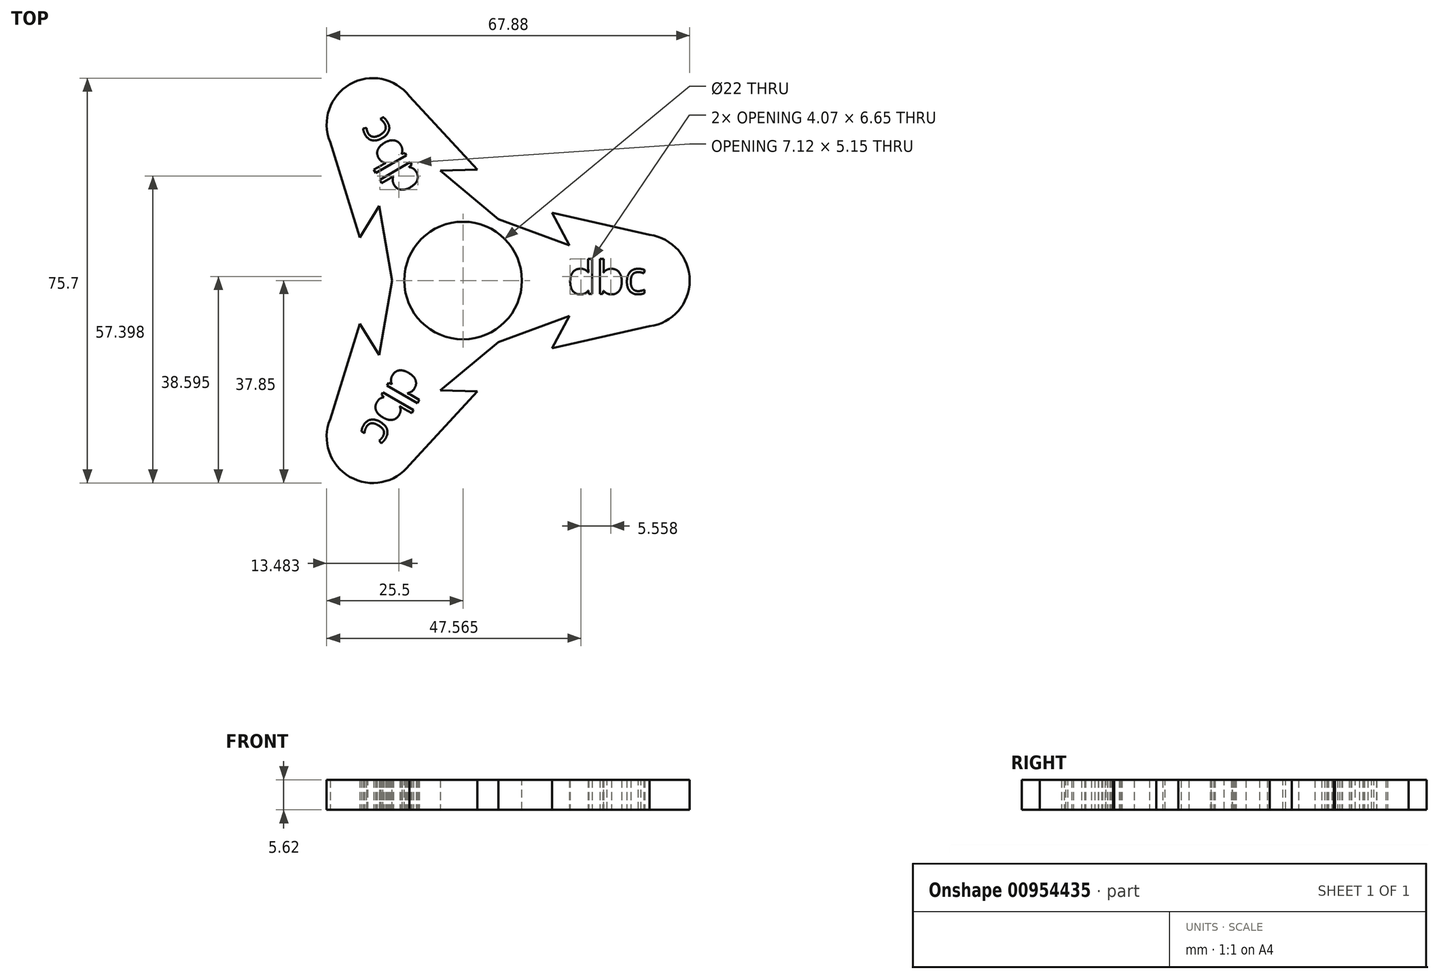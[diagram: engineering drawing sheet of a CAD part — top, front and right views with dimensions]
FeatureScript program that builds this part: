
annotation { "Feature Type Name" : "Feature", "Feature Type Description" : "" }
export const myFeature = defineFeature(function(context is Context, id is Id, definition is map)
    precondition{}
    {
        {
            var Q0;
            Q0=qCreatedBy(makeId("Top.planeOp"),FACE);
            var sketch = newSketch(context, id + "F0", { "sketchPlane" : qUnion([Q0])});
            skCircle(sketch, "E0", {"center": v(0, 0) * mm, "radius": 11 * mm});
            skArc(sketch, "E1", {"start": v(4.51, 16.9) * mm, "mid": v(-17.5, 0) * mm, "end": v(4.51, -16.9) * mm});
            skArc(sketch, "E2", {"start": v(46.5, -11.4) * mm, "mid": v(56.5, 0) * mm, "end": v(46.5, 11.4) * mm});
            skLineSegment(sketch, "E3", {"start": v(0, 17.5) * mm, "end": v(4.51, 16.9) * mm});
            skLineSegment(sketch, "E4", {"start": v(0, -17.5) * mm, "end": v(4.51, -16.9) * mm});
            skLineSegment(sketch, "E5", {"start": v(4.51, -16.9) * mm, "end": v(26.54, -8.8) * mm});
            skLineSegment(sketch, "E6", {"start": v(26.54, -8.8) * mm, "end": v(22.18, -16.9) * mm});
            skLineSegment(sketch, "E7", {"start": v(22.18, -16.9) * mm, "end": v(46.5, -11.4) * mm});
            skLineSegment(sketch, "E8.MirrorCS", {"start": v(4.51, 16.9) * mm, "end": v(26.54, 8.8) * mm});
            skLineSegment(sketch, "E9.MirrorCS", {"start": v(26.54, 8.8) * mm, "end": v(22.18, 16.9) * mm});
            skLineSegment(sketch, "E10.MirrorCS", {"start": v(22.18, 16.9) * mm, "end": v(46.5, 11.4) * mm});
            skText(sketch, "E11", { "text": "dbc\n", "fontName": "OpenSans-Regular.ttf"});
            skLineSegment(sketch, "E12", {"start": v(0, 0) * mm, "end": v(63.02, 0) * mm, "construction": true});
            const initialGuessF0  = {"E11": [0.02606, -0.00333, 1, 0, 0.0083]};
            skSetInitialGuess(sketch, initialGuessF0);
            skSolve(sketch);
        }
        {
            var Q0;
            Q0 = qSketchRegion(id + "F0", true);
            extrude(context, id + "F1", {"entities" : qUnion([Q0]), "endBound" : BoundingType.SYMMETRIC, "depth" : 7.5 * mm, "offsetDistance" : 25 * mm});
        }
        {
            var Q0;
            Q0=makeQuery(id+"F1.opExtrude","SWEPT_BODY",BODY,{"disambiguationData":[OSD([sQuery(id+"F0.wireOp",EDGE,"E0"),sQuery(id+"F0.wireOp",EDGE,"E1"),sQuery(id+"F0.wireOp",EDGE,"E2"),sQuery(id+"F0.wireOp",EDGE,"E3"),sQuery(id+"F0.wireOp",EDGE,"E4")])]});
            var Q1;
            Q1=makeQuery(id+"F1.opExtrude","CAP_EDGE",EDGE,{"disambiguationData":[OSD([sQuery(id+"F0.wireOp",EDGE,"E0")])],"isStart":true});
            circularPattern(context, id + "F2", {"operationType" : NewBodyOperationType.ADD, "entities" : qUnion([Q0]), "axis" : qUnion([Q1]), "angle" : 360 * degree, "instanceCount" : 3, "equalSpace" : true});
        }
        {
            var Q0;
            Q0=makeQuery(id+"F1.opExtrude","SWEPT_BODY",BODY,{"disambiguationData":[OSD([sQuery(id+"F0.wireOp",EDGE,"E0"),sQuery(id+"F0.wireOp",EDGE,"E1"),sQuery(id+"F0.wireOp",EDGE,"E2"),sQuery(id+"F0.wireOp",EDGE,"E5"),sQuery(id+"F0.wireOp",EDGE,"E6"),sQuery(id+"F0.wireOp",EDGE,"E7"),sQuery(id+"F0.wireOp",EDGE,"E8.MirrorCS"),sQuery(id+"F0.wireOp",EDGE,"E9.MirrorCS"),sQuery(id+"F0.wireOp",EDGE,"E10.MirrorCS"),sQuery(id+"F0.wireOp",EDGE,"E11.sketch_text.stroke-0"),sQuery(id+"F0.wireOp",EDGE,"E11.sketch_text.stroke-1"),sQuery(id+"F0.wireOp",EDGE,"E11.sketch_text.stroke-2"),sQuery(id+"F0.wireOp",EDGE,"E11.sketch_text.stroke-3"),sQuery(id+"F0.wireOp",EDGE,"E11.sketch_text.stroke-4"),sQuery(id+"F0.wireOp",EDGE,"E11.sketch_text.stroke-5"),sQuery(id+"F0.wireOp",EDGE,"E11.sketch_text.stroke-6"),sQuery(id+"F0.wireOp",EDGE,"E11.sketch_text.stroke-7"),sQuery(id+"F0.wireOp",EDGE,"E11.sketch_text.stroke-8"),sQuery(id+"F0.wireOp",EDGE,"E11.sketch_text.stroke-9"),sQuery(id+"F0.wireOp",EDGE,"E11.sketch_text.stroke-10"),sQuery(id+"F0.wireOp",EDGE,"E11.sketch_text.stroke-11"),sQuery(id+"F0.wireOp",EDGE,"E11.sketch_text.stroke-12"),sQuery(id+"F0.wireOp",EDGE,"E11.sketch_text.stroke-13"),sQuery(id+"F0.wireOp",EDGE,"E11.sketch_text.stroke-14"),sQuery(id+"F0.wireOp",EDGE,"E11.sketch_text.stroke-24"),sQuery(id+"F0.wireOp",EDGE,"E11.sketch_text.stroke-25"),sQuery(id+"F0.wireOp",EDGE,"E11.sketch_text.stroke-26"),sQuery(id+"F0.wireOp",EDGE,"E11.sketch_text.stroke-27"),sQuery(id+"F0.wireOp",EDGE,"E11.sketch_text.stroke-28"),sQuery(id+"F0.wireOp",EDGE,"E11.sketch_text.stroke-29"),sQuery(id+"F0.wireOp",EDGE,"E11.sketch_text.stroke-30"),sQuery(id+"F0.wireOp",EDGE,"E11.sketch_text.stroke-31"),sQuery(id+"F0.wireOp",EDGE,"E11.sketch_text.stroke-32"),sQuery(id+"F0.wireOp",EDGE,"E11.sketch_text.stroke-33"),sQuery(id+"F0.wireOp",EDGE,"E11.sketch_text.stroke-34"),sQuery(id+"F0.wireOp",EDGE,"E11.sketch_text.stroke-35"),sQuery(id+"F0.wireOp",EDGE,"E11.sketch_text.stroke-36"),sQuery(id+"F0.wireOp",EDGE,"E11.sketch_text.stroke-37"),sQuery(id+"F0.wireOp",EDGE,"E11.sketch_text.stroke-38"),sQuery(id+"F0.wireOp",EDGE,"E11.sketch_text.stroke-47"),sQuery(id+"F0.wireOp",EDGE,"E11.sketch_text.stroke-48"),sQuery(id+"F0.wireOp",EDGE,"E11.sketch_text.stroke-49"),sQuery(id+"F0.wireOp",EDGE,"E11.sketch_text.stroke-50"),sQuery(id+"F0.wireOp",EDGE,"E11.sketch_text.stroke-51"),sQuery(id+"F0.wireOp",EDGE,"E11.sketch_text.stroke-52"),sQuery(id+"F0.wireOp",EDGE,"E11.sketch_text.stroke-53"),sQuery(id+"F0.wireOp",EDGE,"E11.sketch_text.stroke-54"),sQuery(id+"F0.wireOp",EDGE,"E11.sketch_text.stroke-55"),sQuery(id+"F0.wireOp",EDGE,"E11.sketch_text.stroke-56"),sQuery(id+"F0.wireOp",EDGE,"E11.sketch_text.stroke-57"),sQuery(id+"F0.wireOp",EDGE,"E11.sketch_text.stroke-58"),sQuery(id+"F0.wireOp",EDGE,"E11.sketch_text.stroke-59"),sQuery(id+"F0.wireOp",EDGE,"E11.sketch_text.stroke-60"),sQuery(id+"F0.wireOp",EDGE,"E11.sketch_text.stroke-61")])]});
            var Q1;
            Q1=sQuery(id+"F0.wireOp",VERTEX,"E0.center");
            var Q2;
            Q2=sQuery(id+"F0.wireOp",VERTEX,"E0.center");
            transform(context, id + "F3", {"entities" : qUnion([Q0]), "transformType" : TransformType.SCALE_UNIFORMLY, "scale" : .75, "scalePoint" : qUnion([Q2]), "makeCopy" : false});
        }
        {
            var Q0;
            {var subQ0=makeQuery(id+"F1.opExtrude","CAP_FACE",FACE,{"disambiguationData":[OSD([sQuery(id+"F0.wireOp",EDGE,"E0"),sQuery(id+"F0.wireOp",EDGE,"E1"),sQuery(id+"F0.wireOp",EDGE,"E2"),sQuery(id+"F0.wireOp",EDGE,"E5"),sQuery(id+"F0.wireOp",EDGE,"E6"),sQuery(id+"F0.wireOp",EDGE,"E7"),sQuery(id+"F0.wireOp",EDGE,"E8.MirrorCS"),sQuery(id+"F0.wireOp",EDGE,"E9.MirrorCS"),sQuery(id+"F0.wireOp",EDGE,"E10.MirrorCS"),sQuery(id+"F0.wireOp",EDGE,"E11.sketch_text.stroke-0"),sQuery(id+"F0.wireOp",EDGE,"E11.sketch_text.stroke-1"),sQuery(id+"F0.wireOp",EDGE,"E11.sketch_text.stroke-2"),sQuery(id+"F0.wireOp",EDGE,"E11.sketch_text.stroke-3"),sQuery(id+"F0.wireOp",EDGE,"E11.sketch_text.stroke-4"),sQuery(id+"F0.wireOp",EDGE,"E11.sketch_text.stroke-5"),sQuery(id+"F0.wireOp",EDGE,"E11.sketch_text.stroke-6"),sQuery(id+"F0.wireOp",EDGE,"E11.sketch_text.stroke-7"),sQuery(id+"F0.wireOp",EDGE,"E11.sketch_text.stroke-8"),sQuery(id+"F0.wireOp",EDGE,"E11.sketch_text.stroke-9"),sQuery(id+"F0.wireOp",EDGE,"E11.sketch_text.stroke-10"),sQuery(id+"F0.wireOp",EDGE,"E11.sketch_text.stroke-11"),sQuery(id+"F0.wireOp",EDGE,"E11.sketch_text.stroke-12"),sQuery(id+"F0.wireOp",EDGE,"E11.sketch_text.stroke-13"),sQuery(id+"F0.wireOp",EDGE,"E11.sketch_text.stroke-14"),sQuery(id+"F0.wireOp",EDGE,"E11.sketch_text.stroke-24"),sQuery(id+"F0.wireOp",EDGE,"E11.sketch_text.stroke-25"),sQuery(id+"F0.wireOp",EDGE,"E11.sketch_text.stroke-26"),sQuery(id+"F0.wireOp",EDGE,"E11.sketch_text.stroke-27"),sQuery(id+"F0.wireOp",EDGE,"E11.sketch_text.stroke-28"),sQuery(id+"F0.wireOp",EDGE,"E11.sketch_text.stroke-29"),sQuery(id+"F0.wireOp",EDGE,"E11.sketch_text.stroke-30"),sQuery(id+"F0.wireOp",EDGE,"E11.sketch_text.stroke-31"),sQuery(id+"F0.wireOp",EDGE,"E11.sketch_text.stroke-32"),sQuery(id+"F0.wireOp",EDGE,"E11.sketch_text.stroke-33"),sQuery(id+"F0.wireOp",EDGE,"E11.sketch_text.stroke-34"),sQuery(id+"F0.wireOp",EDGE,"E11.sketch_text.stroke-35"),sQuery(id+"F0.wireOp",EDGE,"E11.sketch_text.stroke-36"),sQuery(id+"F0.wireOp",EDGE,"E11.sketch_text.stroke-37"),sQuery(id+"F0.wireOp",EDGE,"E11.sketch_text.stroke-38"),sQuery(id+"F0.wireOp",EDGE,"E11.sketch_text.stroke-47"),sQuery(id+"F0.wireOp",EDGE,"E11.sketch_text.stroke-48"),sQuery(id+"F0.wireOp",EDGE,"E11.sketch_text.stroke-49"),sQuery(id+"F0.wireOp",EDGE,"E11.sketch_text.stroke-50"),sQuery(id+"F0.wireOp",EDGE,"E11.sketch_text.stroke-51"),sQuery(id+"F0.wireOp",EDGE,"E11.sketch_text.stroke-52"),sQuery(id+"F0.wireOp",EDGE,"E11.sketch_text.stroke-53"),sQuery(id+"F0.wireOp",EDGE,"E11.sketch_text.stroke-54"),sQuery(id+"F0.wireOp",EDGE,"E11.sketch_text.stroke-55"),sQuery(id+"F0.wireOp",EDGE,"E11.sketch_text.stroke-56"),sQuery(id+"F0.wireOp",EDGE,"E11.sketch_text.stroke-57"),sQuery(id+"F0.wireOp",EDGE,"E11.sketch_text.stroke-58"),sQuery(id+"F0.wireOp",EDGE,"E11.sketch_text.stroke-59"),sQuery(id+"F0.wireOp",EDGE,"E11.sketch_text.stroke-60"),sQuery(id+"F0.wireOp",EDGE,"E11.sketch_text.stroke-61")])],"isStart":false});Q0=makeQuery(id+"F2.boolean.opBoolean","MERGE",FACE,{"derivedFrom":[subQ0,makeQuery(id+"F2.opPattern","COPY",FACE,{"derivedFrom":subQ0,"instanceName":"1"}),makeQuery(id+"F2.opPattern","COPY",FACE,{"derivedFrom":subQ0,"instanceName":"2"})]});}
            var sketch = newSketch(context, id + "F4", { "sketchPlane" : qUnion([Q0])});
            skPoint(sketch, "E13.0", {"position": v(0, 0) * mm});
            skCircle(sketch, "E14", {"center": v(0, 0) * mm, "radius": 11 * mm});
            skSolve(sketch);
        }
        {
            var Q0;
            Q0 = qSketchRegion(id + "F4", true);
            extrude(context, id + "F5", {"entities" : qUnion([Q0]), "operationType" : NewBodyOperationType.REMOVE, "oppositeDirection" : true, "depth" : 25 * mm, "offsetDistance" : 25 * mm});
        }
    });
